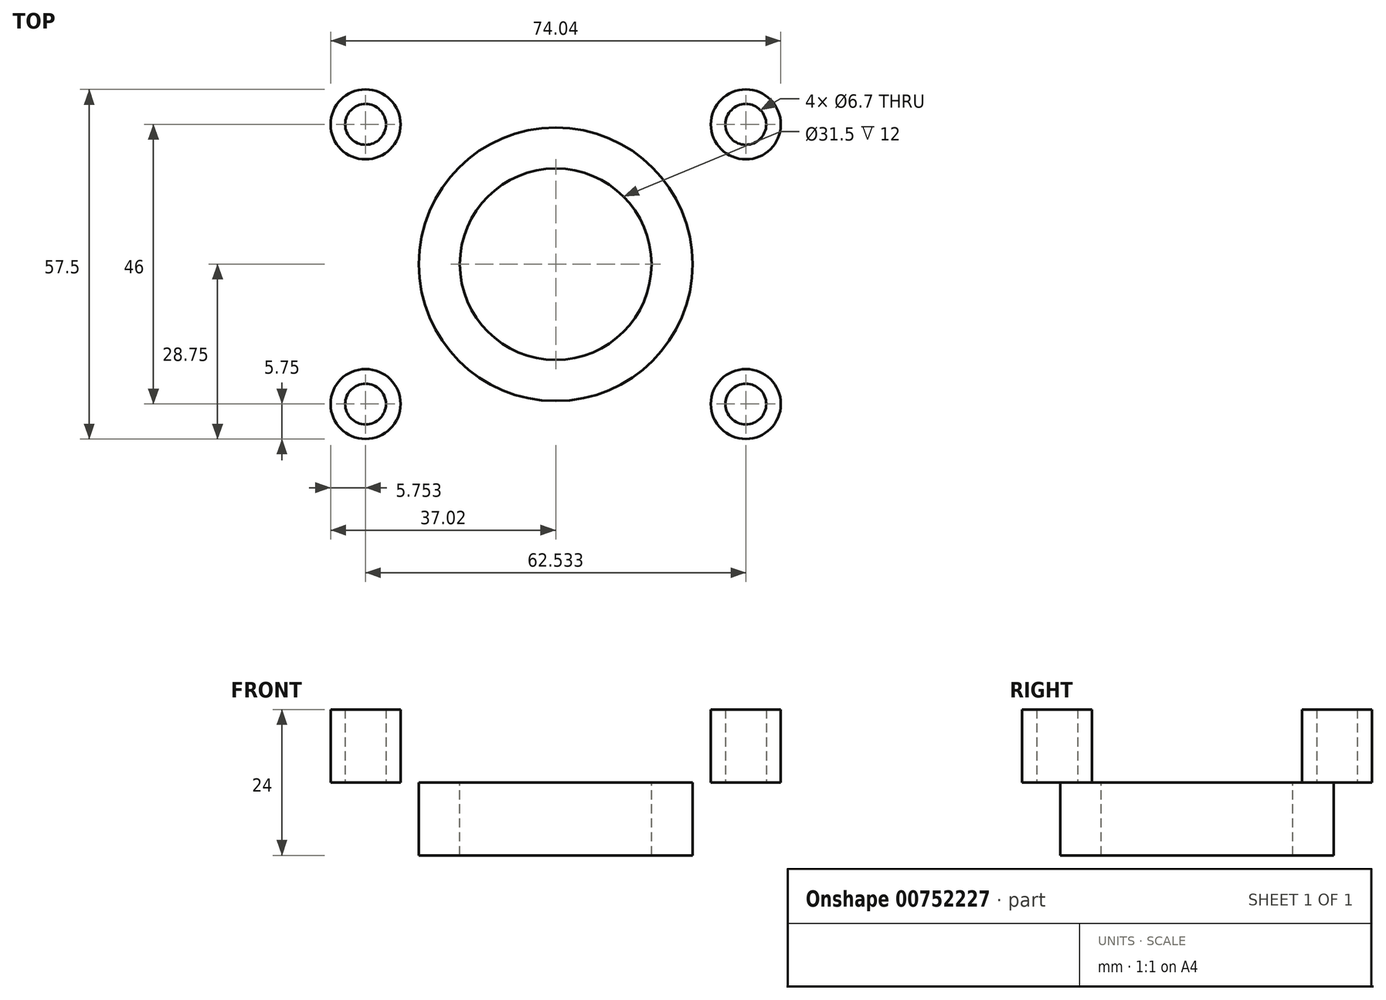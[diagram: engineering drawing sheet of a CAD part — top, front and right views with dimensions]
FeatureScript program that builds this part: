
annotation { "Feature Type Name" : "Feature", "Feature Type Description" : "" }
export const myFeature = defineFeature(function(context is Context, id is Id, definition is map)
    precondition{}
    {
        {
            var Q0;
            Q0=qCreatedBy(makeId("Top.planeOp"),FACE);
            var sketch = newSketch(context, id + "F0", { "sketchPlane" : qUnion([Q0])});
            skCircle(sketch, "E0", {"center": v(-31.27, 23) * mm, "radius": 5.75 * mm});
            skCircle(sketch, "E1", {"center": v(31.27, -23) * mm, "radius": 5.75 * mm});
            skCircle(sketch, "E2", {"center": v(31.27, -23) * mm, "radius": 3.35 * mm});
            skCircle(sketch, "E3", {"center": v(-31.27, 23) * mm, "radius": 3.35 * mm});
            skLineSegment(sketch, "E4", {"start": v(-31.27, 23) * mm, "end": v(31.27, -23) * mm});
            skCircle(sketch, "E5", {"center": v(0, 0) * mm, "radius": 22.5 * mm});
            skCircle(sketch, "E6", {"center": v(0, 0) * mm, "radius": 15.75 * mm});
            skLineSegment(sketch, "E7", {"start": v(-31.27, 23) * mm, "end": v(-31.27, -23) * mm});
            skLineSegment(sketch, "E8", {"start": v(-31.27, -23) * mm, "end": v(31.27, -23) * mm});
            skCircle(sketch, "E9", {"center": v(-31.27, -23) * mm, "radius": 5.75 * mm});
            skCircle(sketch, "E10", {"center": v(-31.27, -23) * mm, "radius": 3.35 * mm});
            skLineSegment(sketch, "E11", {"start": v(-31.27, 23) * mm, "end": v(31.27, 23) * mm});
            skCircle(sketch, "E12", {"center": v(31.27, 23) * mm, "radius": 5.75 * mm});
            skCircle(sketch, "E13", {"center": v(31.27, 23) * mm, "radius": 3.35 * mm});
            skLineSegment(sketch, "E14", {"start": v(31.27, -23) * mm, "end": v(31.27, 23) * mm});
            skSolve(sketch);
        }
        {
            var Q0;
            {var subQ0=sQuery(id+"F0.wireOp",EDGE,"E9");var subQ1=sQuery(id+"F0.wireOp",EDGE,"E7");var subQ2=makeQuery(id+"F0.imprint","INTERSECT",VERTEX,{"derivedFrom":[subQ1,subQ0]});Q0=makeQuery(id+"F0.imprint","IMPRINT",FACE,{"disambiguationData":[TD([[makeQuery(id+"F0.imprint","IMPRINT",EDGE,{"disambiguationData":[TD([[subQ2,-1.0]])],"derivedFrom":subQ1}),-1.0]])]});}
            var Q1;
            {var subQ0=sQuery(id+"F0.wireOp",EDGE,"E12");var subQ1=sQuery(id+"F0.wireOp",EDGE,"E11");var subQ2=makeQuery(id+"F0.imprint","INTERSECT",VERTEX,{"derivedFrom":[subQ1,subQ0]});Q1=makeQuery(id+"F0.imprint","IMPRINT",FACE,{"disambiguationData":[TD([[makeQuery(id+"F0.imprint","IMPRINT",EDGE,{"disambiguationData":[TD([[subQ2,-1.0]])],"derivedFrom":subQ1}),1.0]])]});}
            var Q2;
            {var subQ0=sQuery(id+"F0.wireOp",EDGE,"E7");var subQ1=sQuery(id+"F0.wireOp",EDGE,"E0");var subQ2=makeQuery(id+"F0.imprint","INTERSECT",VERTEX,{"derivedFrom":[subQ1,subQ0]});Q2=makeQuery(id+"F0.imprint","IMPRINT",FACE,{"disambiguationData":[TD([[makeQuery(id+"F0.imprint","IMPRINT",EDGE,{"disambiguationData":[TD([[subQ2,1.0]])],"derivedFrom":subQ1}),1.0]])]});}
            var Q3;
            {var subQ0=sQuery(id+"F0.wireOp",EDGE,"E14");var subQ1=sQuery(id+"F0.wireOp",EDGE,"E1");var subQ2=makeQuery(id+"F0.imprint","INTERSECT",VERTEX,{"derivedFrom":[subQ1,subQ0]});Q3=makeQuery(id+"F0.imprint","IMPRINT",FACE,{"disambiguationData":[TD([[makeQuery(id+"F0.imprint","IMPRINT",EDGE,{"disambiguationData":[TD([[subQ2,1.0]])],"derivedFrom":subQ1}),1.0]])]});}
            var Q4;
            {var subQ0=sQuery(id+"F0.wireOp",EDGE,"E9");var subQ1=sQuery(id+"F0.wireOp",EDGE,"E7");var subQ2=makeQuery(id+"F0.imprint","INTERSECT",VERTEX,{"derivedFrom":[subQ1,subQ0]});Q4=makeQuery(id+"F0.imprint","IMPRINT",FACE,{"disambiguationData":[TD([[makeQuery(id+"F0.imprint","IMPRINT",EDGE,{"disambiguationData":[TD([[subQ2,-1.0]])],"derivedFrom":subQ1}),1.0]])]});}
            var Q5;
            {var subQ0=sQuery(id+"F0.wireOp",EDGE,"E12");var subQ1=sQuery(id+"F0.wireOp",EDGE,"E11");var subQ2=makeQuery(id+"F0.imprint","INTERSECT",VERTEX,{"derivedFrom":[subQ1,subQ0]});Q5=makeQuery(id+"F0.imprint","IMPRINT",FACE,{"disambiguationData":[TD([[makeQuery(id+"F0.imprint","IMPRINT",EDGE,{"disambiguationData":[TD([[subQ2,-1.0]])],"derivedFrom":subQ1}),-1.0]])]});}
            var Q6;
            {var subQ0=sQuery(id+"F0.wireOp",EDGE,"E7");var subQ1=sQuery(id+"F0.wireOp",EDGE,"E0");var subQ2=makeQuery(id+"F0.imprint","INTERSECT",VERTEX,{"derivedFrom":[subQ1,subQ0]});Q6=makeQuery(id+"F0.imprint","IMPRINT",FACE,{"disambiguationData":[TD([[makeQuery(id+"F0.imprint","IMPRINT",EDGE,{"disambiguationData":[TD([[subQ2,-1.0]])],"derivedFrom":subQ1}),1.0]])]});}
            var Q7;
            {var subQ0=sQuery(id+"F0.wireOp",EDGE,"E11");var subQ1=sQuery(id+"F0.wireOp",EDGE,"E0");var subQ2=makeQuery(id+"F0.imprint","INTERSECT",VERTEX,{"derivedFrom":[subQ1,subQ0]});Q7=makeQuery(id+"F0.imprint","IMPRINT",FACE,{"disambiguationData":[TD([[makeQuery(id+"F0.imprint","IMPRINT",EDGE,{"disambiguationData":[TD([[subQ2,1.0]])],"derivedFrom":subQ1}),1.0]])]});}
            var Q8;
            {var subQ0=sQuery(id+"F0.wireOp",EDGE,"E14");var subQ1=sQuery(id+"F0.wireOp",EDGE,"E1");var subQ2=makeQuery(id+"F0.imprint","INTERSECT",VERTEX,{"derivedFrom":[subQ1,subQ0]});Q8=makeQuery(id+"F0.imprint","IMPRINT",FACE,{"disambiguationData":[TD([[makeQuery(id+"F0.imprint","IMPRINT",EDGE,{"disambiguationData":[TD([[subQ2,-1.0]])],"derivedFrom":subQ1}),1.0]])]});}
            var Q9;
            {var subQ0=sQuery(id+"F0.wireOp",EDGE,"E8");var subQ1=sQuery(id+"F0.wireOp",EDGE,"E1");var subQ2=makeQuery(id+"F0.imprint","INTERSECT",VERTEX,{"derivedFrom":[subQ1,subQ0]});Q9=makeQuery(id+"F0.imprint","IMPRINT",FACE,{"disambiguationData":[TD([[makeQuery(id+"F0.imprint","IMPRINT",EDGE,{"disambiguationData":[TD([[subQ2,1.0]])],"derivedFrom":subQ1}),1.0]])]});}
            extrude(context, id + "F1", {"entities" : qUnion([Q0, Q1, Q2, Q3, Q4, Q5, Q6, Q7, Q8, Q9]), "depth" : 12 * mm, "offsetDistance" : 25 * mm});
        }
        {
            var Q0;
            {var subQ0=sQuery(id+"F0.wireOp",EDGE,"E5");var subQ1=sQuery(id+"F0.wireOp",EDGE,"E4");var subQ2=makeQuery(id+"F0.imprint","INTERSECT",VERTEX,{"disambiguationData":[OD(0.0)],"derivedFrom":[subQ1,subQ0]});Q0=makeQuery(id+"F0.imprint","IMPRINT",FACE,{"disambiguationData":[TD([[makeQuery(id+"F0.imprint","IMPRINT",EDGE,{"disambiguationData":[TD([[subQ2,-1.0]])],"derivedFrom":subQ1}),1.0]])]});}
            var Q1;
            {var subQ0=sQuery(id+"F0.wireOp",EDGE,"E5");var subQ1=sQuery(id+"F0.wireOp",EDGE,"E4");var subQ2=makeQuery(id+"F0.imprint","INTERSECT",VERTEX,{"disambiguationData":[OD(0.0)],"derivedFrom":[subQ1,subQ0]});Q1=makeQuery(id+"F0.imprint","IMPRINT",FACE,{"disambiguationData":[TD([[makeQuery(id+"F0.imprint","IMPRINT",EDGE,{"disambiguationData":[TD([[subQ2,-1.0]])],"derivedFrom":subQ1}),-1.0]])]});}
            extrude(context, id + "F2", {"entities" : qUnion([Q0, Q1]), "depth" : -12 * mm, "offsetDistance" : 25 * mm});
        }
    });
